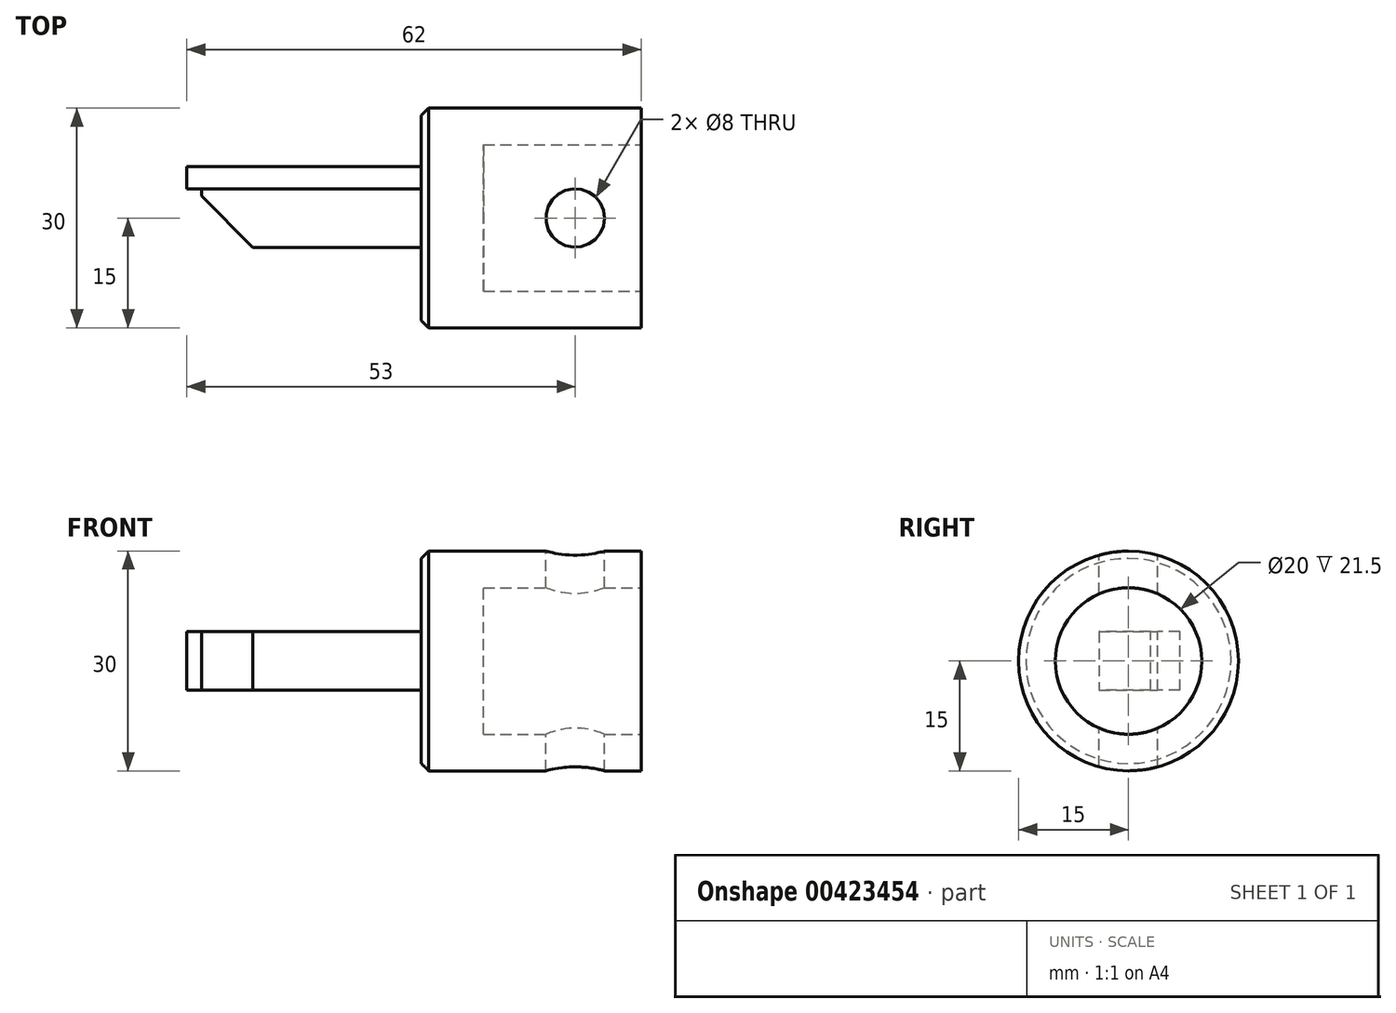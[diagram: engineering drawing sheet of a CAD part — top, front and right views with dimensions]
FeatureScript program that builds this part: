
annotation { "Feature Type Name" : "Feature", "Feature Type Description" : "" }
export const myFeature = defineFeature(function(context is Context, id is Id, definition is map)
    precondition{}
    {
        {
            var Q0;
            Q0=qCreatedBy(makeId("Right.planeOp"),FACE);
            var sketch = newSketch(context, id + "F0", { "sketchPlane" : qUnion([Q0])});
            skCircle(sketch, "E0", {"center": v(0, 0) * mm, "radius": 15 * mm});
            skSolve(sketch);
        }
        {
            var Q0;
            Q0=makeQuery(id+"F0.imprint","IMPRINT",FACE,{"disambiguationData":[TD([[makeQuery(id+"F0.imprint","IMPRINT",EDGE,{"derivedFrom":sQuery(id+"F0.wireOp",EDGE,"E0")}),1.0]])]});
            extrude(context, id + "F1", {"entities" : qUnion([Q0]), "depth" : 30 * mm});
        }
        {
            var Q0;
            Q0=makeQuery(id+"F1.opExtrude","CAP_FACE",FACE,{"disambiguationData":[OSD([sQuery(id+"F0.wireOp",EDGE,"E0")])],"isStart":false});
            var sketch = newSketch(context, id + "F2", { "sketchPlane" : qUnion([Q0])});
            skCircle(sketch, "E1", {"center": v(0, 0) * mm, "radius": 10 * mm});
            skSolve(sketch);
        }
        {
            var Q0;
            Q0 = qSketchRegion(id + "F2", true);
            extrude(context, id + "F3", {"entities" : qUnion([Q0]), "operationType" : NewBodyOperationType.REMOVE, "oppositeDirection" : true, "depth" : 21.5 * mm});
        }
        {
            var Q0;
            Q0=qCreatedBy(makeId("Top.planeOp"),FACE);
            cPlane(context, id + "F4", {"entities" : qUnion([Q0]), "cplaneType" : CPlaneType.OFFSET, "offset" : 15 * mm, "width" : 150 * mm, "height" : 150 * mm});
        }
        {
            var Q0;
            Q0=qCreatedBy(id+"F4.planeOp",FACE);
            var sketch = newSketch(context, id + "F5", { "sketchPlane" : qUnion([Q0])});
            skCircle(sketch, "E2", {"center": v(21, 0) * mm, "radius": 4 * mm});
            skSolve(sketch);
        }
        {
            var Q0;
            Q0 = qSketchRegion(id + "F5", true);
            extrude(context, id + "F6", {"entities" : qUnion([Q0]), "operationType" : NewBodyOperationType.REMOVE, "endBound" : BoundingType.THROUGH_ALL, "oppositeDirection" : true, "depth" : 25 * mm});
        }
        {
            var Q0;
            Q0=qCreatedBy(makeId("Right.planeOp"),FACE);
            var sketch = newSketch(context, id + "F7", { "sketchPlane" : qUnion([Q0])});
            skLineSegment(sketch, "E3.bottom", {"start": v(-4, 4) * mm, "end": v(4, 4) * mm});
            skLineSegment(sketch, "E3.top", {"start": v(-4, -4) * mm, "end": v(4, -4) * mm});
            skLineSegment(sketch, "E3.left", {"start": v(-4, 4) * mm, "end": v(-4, -4) * mm});
            skLineSegment(sketch, "E3.right", {"start": v(4, 4) * mm, "end": v(4, -4) * mm});
            skPoint(sketch, "E3.middle", {"position": v(0, 0) * mm});
            skSolve(sketch);
        }
        {
            var Q0;
            Q0 = qSketchRegion(id + "F7", true);
            extrude(context, id + "F8", {"entities" : qUnion([Q0]), "operationType" : NewBodyOperationType.ADD, "oppositeDirection" : true, "depth" : 30 * mm, "offsetDistance" : 25 * mm});
        }
        {
            var Q0;
            Q0=qCreatedBy(makeId("Top.planeOp"),FACE);
            var sketch = newSketch(context, id + "F9", { "sketchPlane" : qUnion([Q0])});
            skLineSegment(sketch, "E4", {"start": v(-30, 3) * mm, "end": v(-23, -4) * mm});
            skLineSegment(sketch, "E5", {"start": v(-23, -4) * mm, "end": v(-30, -4) * mm});
            skLineSegment(sketch, "E6", {"start": v(-30, -4) * mm, "end": v(-30, 3) * mm});
            skSolve(sketch);
        }
        {
            var Q0;
            Q0 = qSketchRegion(id + "F9", true);
            extrude(context, id + "F10", {"entities" : qUnion([Q0]), "operationType" : NewBodyOperationType.REMOVE, "endBound" : BoundingType.UP_TO_NEXT, "oppositeDirection" : true, "depth" : 25 * mm, "hasSecondDirection" : true, "secondDirectionBound" : SecondDirectionBoundingType.UP_TO_NEXT, "secondDirectionOppositeDirection" : false, "secondDirectionDepth" : 25 * mm});
        }
        {
            var Q0;
            Q0=makeQuery(id+"F1.opExtrude","CAP_EDGE",EDGE,{"disambiguationData":[OSD([sQuery(id+"F0.wireOp",EDGE,"E0")])],"isStart":true});
            chamfer(context, id + "F11", {"entities" : qUnion([Q0]), "width" : 1 * mm, "tangentPropagation" : true});
        }
        {
            var Q0;
            Q0=makeQuery(id+"F8.opExtrude","SWEPT_FACE",FACE,{"disambiguationData":[OSD([sQuery(id+"F7.wireOp",EDGE,"E3.right")])]});
            var sketch = newSketch(context, id + "F12", { "sketchPlane" : qUnion([Q0])});
            skLineSegment(sketch, "E7.bottom", {"start": v(32, -4) * mm, "end": v(0, -4) * mm});
            skLineSegment(sketch, "E7.top", {"start": v(32, 4) * mm, "end": v(0, 4) * mm});
            skLineSegment(sketch, "E7.left", {"start": v(32, -4) * mm, "end": v(32, 4) * mm});
            skLineSegment(sketch, "E7.right", {"start": v(0, -4) * mm, "end": v(0, 4) * mm});
            skSolve(sketch);
        }
        {
            var Q0;
            Q0 = qSketchRegion(id + "F12", true);
            extrude(context, id + "F13", {"entities" : qUnion([Q0]), "depth" : 3 * mm, "offsetDistance" : 25 * mm});
        }
    });
